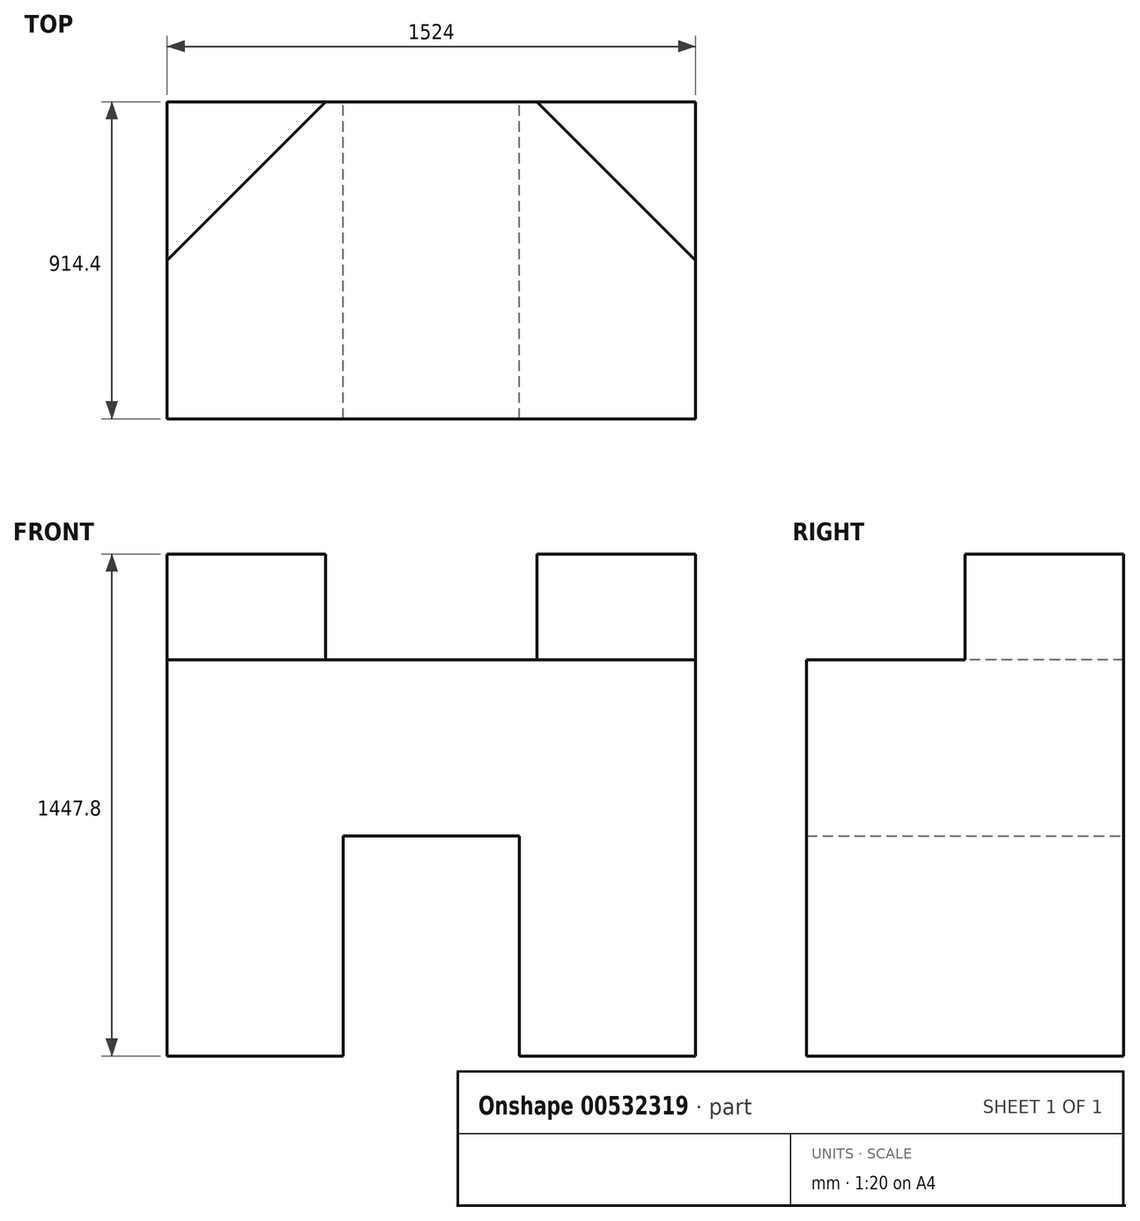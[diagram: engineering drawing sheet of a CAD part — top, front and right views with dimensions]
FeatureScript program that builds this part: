
annotation { "Feature Type Name" : "Feature", "Feature Type Description" : "" }
export const myFeature = defineFeature(function(context is Context, id is Id, definition is map)
    precondition{}
    {
        {
            var Q0;
            Q0=qCreatedBy(makeId("Front.planeOp"),FACE);
            var sketch = newSketch(context, id + "F0", { "sketchPlane" : qUnion([Q0])});
            skLineSegment(sketch, "E0.bottom", {"start": v(762, -571.5) * mm, "end": v(254, -571.5) * mm});
            skLineSegment(sketch, "E0.top", {"start": v(762, 571.5) * mm, "end": v(-762, 571.5) * mm});
            skLineSegment(sketch, "E0.left", {"start": v(762, -571.5) * mm, "end": v(762, 571.5) * mm});
            skLineSegment(sketch, "E0.right", {"start": v(-762, -571.5) * mm, "end": v(-762, 571.5) * mm});
            skPoint(sketch, "E0.middle", {"position": v(0, 0) * mm});
            skLineSegment(sketch, "E1.top", {"start": v(254, 63.5) * mm, "end": v(-254, 63.5) * mm});
            skLineSegment(sketch, "E1.left", {"start": v(254, -571.5) * mm, "end": v(254, 63.5) * mm});
            skLineSegment(sketch, "E1.right", {"start": v(-254, -571.5) * mm, "end": v(-254, 63.5) * mm});
            skLineSegment(sketch, "E2.trimOffspring", {"start": v(-254, -571.5) * mm, "end": v(-762, -571.5) * mm});
            skSolve(sketch);
        }
        {
            var Q0;
            Q0 = qSketchRegion(id + "F0", true);
            extrude(context, id + "F1", {"entities" : qUnion([Q0]), "depth" : 914.4 * mm, "offsetDistance" : 25.4 * mm});
        }
        {
            var Q0;
            Q0=makeQuery(id+"F1.opExtrude","SWEPT_FACE",FACE,{"disambiguationData":[OSD([sQuery(id+"F0.wireOp",EDGE,"E0.top")])]});
            var sketch = newSketch(context, id + "F2", { "sketchPlane" : qUnion([Q0])});
            skLineSegment(sketch, "E3", {"start": v(-762, 0) * mm, "end": v(-304.8, 0) * mm});
            skLineSegment(sketch, "E4", {"start": v(-304.8, 0) * mm, "end": v(-762, -457.2) * mm});
            skLineSegment(sketch, "E5", {"start": v(-762, -457.2) * mm, "end": v(-762, 0) * mm});
            skLineSegment(sketch, "E6", {"start": v(762, 0) * mm, "end": v(304.8, 0) * mm});
            skLineSegment(sketch, "E7", {"start": v(304.8, 0) * mm, "end": v(762, -457.2) * mm});
            skLineSegment(sketch, "E8", {"start": v(762, -457.2) * mm, "end": v(762, 0) * mm});
            skSolve(sketch);
        }
        {
            var Q0;
            Q0=makeQuery(id+"F2.imprint","IMPRINT",FACE,{"disambiguationData":[TD([[makeQuery(id+"F2.imprint","IMPRINT",EDGE,{"derivedFrom":sQuery(id+"F2.wireOp",EDGE,"E3")}),1.0]])]});
            var Q1;
            Q1=makeQuery(id+"F2.imprint","IMPRINT",FACE,{"disambiguationData":[TD([[makeQuery(id+"F2.imprint","IMPRINT",EDGE,{"derivedFrom":sQuery(id+"F2.wireOp",EDGE,"E6")}),1.0]])]});
            extrude(context, id + "F3", {"entities" : qUnion([Q0, Q1]), "operationType" : NewBodyOperationType.ADD, "depth" : 304.8 * mm, "offsetDistance" : 25.4 * mm});
        }
    });
